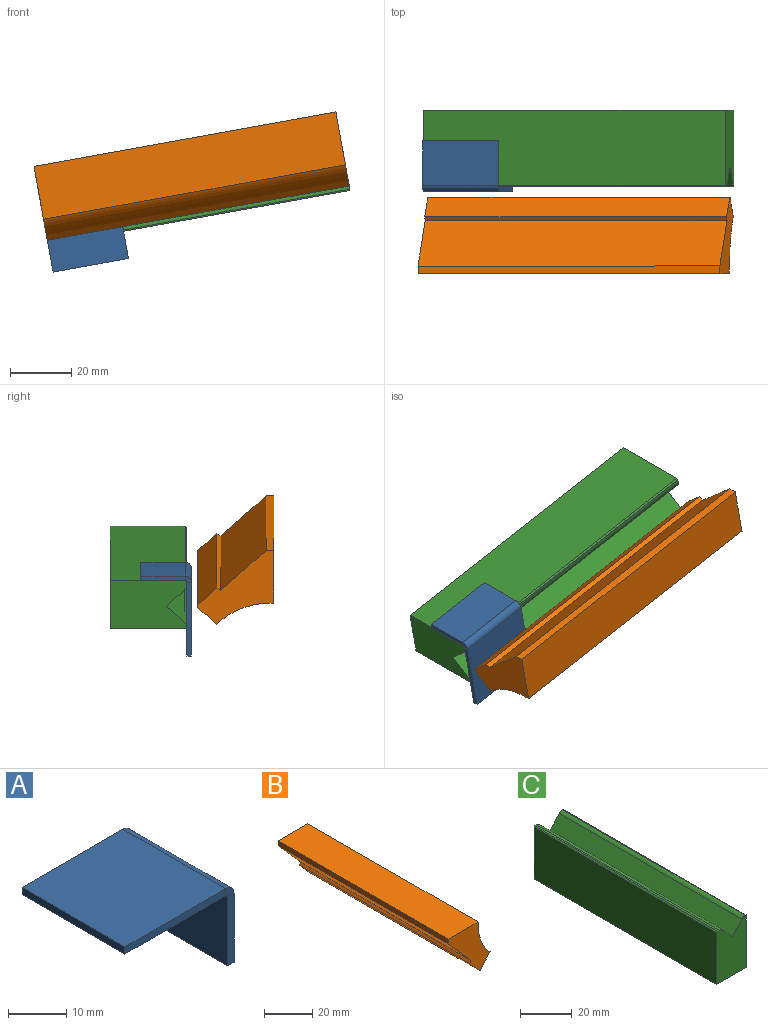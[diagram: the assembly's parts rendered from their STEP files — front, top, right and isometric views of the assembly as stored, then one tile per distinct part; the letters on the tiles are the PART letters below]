
ASSEMBLY  parts=3 mates=5
PART A: 14 faces, bbox 26.5x25x16.5 mm
  f0: plane 24.5x1.5mm, normal (0,1,0), area 36.8mm2, adj f2,f3,f4,f11
  f1: plane 24.5x1.5mm, normal (0,-1,0), area 36.8mm2, adj f2,f3,f4,f10
  f2: plane 25x1.5mm, normal (-1,0,0), area 37.5mm2, adj f0,f1,f3,f4
  f3: plane 25x24.5mm, normal (0,0,-1), area 612.5mm2, adj f0,f1,f2,f13
  f4: plane 25x24.5mm, normal (0,0,1), area 612.5mm2, adj f0,f1,f2,f12
  f5: plane 14.5x1.5mm, normal (0,1,0), area 21.7mm2, adj f6,f8,f9,f11
  f6: plane 25x1.5mm, normal (0,0,-1), area 37.5mm2, adj f5,f7,f8,f9
  f7: plane 14.5x1.5mm, normal (0,-1,0), area 21.7mm2, adj f6,f8,f9,f10
  f8: plane 25x14.5mm, normal (-1,0,0), area 362.5mm2, adj f5,f6,f7,f13
  f9: plane 25x14.5mm, normal (1,0,0), area 362.5mm2, adj f5,f6,f7,f12
  f10: plane 2x2mm, normal (0,-1,0), area 2.9mm2, adj f1,f7,f12,f13
  f11: plane 2x2mm, normal (0,1,0), area 2.9mm2, adj f0,f5,f12,f13
  f12: cylinder r=2mm len=25mm, axis (0,-1,0), area 78.5mm2, adj f4,f9,f10,f11
  f13: cylinder r=0.5mm len=25mm, axis (0,-1,0), area 19.6mm2, adj f3,f8,f10,f11
PART B: 11 faces, bbox 24.5x100x25 mm
  f0: cylinder r=0.6mm len=100mm, axis (0,1,0), area 100.5mm2, adj f1,f7,f8,f9
  f1: plane 100x6.16mm, normal (0.74,0,-0.67), area 829.1mm2, adj f0,f2,f8,f9
  f2: cylinder r=25mm len=100mm, axis (0,1,0), area 1916.6mm2, adj f1,f3,f8,f9
  f3: plane 100x1.3mm, normal (1,0,0), area 129.7mm2, adj f2,f8,f9,f10
  f4: plane 100x2.51mm, normal (-1,0,0), area 250.9mm2, adj f5,f8,f9,f10
  f5: plane 100x14.8mm, normal (-0.74,0,-0.67), area 1991.2mm2, adj f4,f6,f8,f9
  f6: plane 100x1.3mm, normal (-0.84,0,0.54), area 155.3mm2, adj f5,f7,f8,f9
  f7: plane 100x6.19mm, normal (-0.74,0,-0.67), area 833.4mm2, adj f0,f6,f8,f9
  f8: plane 25x24.49mm, normal (0,-1,0), area 288.1mm2, adj f0,f1,f2,f3,f4,f5,f6,f7
  f9: plane 25x24.49mm, normal (0,1,0), area 288.1mm2, adj f0,f1,f2,f3,f4,f5,f6,f7
  f10: plane 100x17.5mm, normal (0,0,1), area 1750mm2, adj f3,f4,f8,f9
PART C: 12 faces, bbox 16x100x25 mm
  f0: plane 100x25mm, normal (1,0,0), area 2500mm2, adj f2,f3,f4,f11
  f1: plane 100x24.5mm, normal (-1,0,0), area 2450mm2, adj f2,f3,f10,f11
  f2: plane 25x16mm, normal (0,-1,0), area 359.6mm2, adj f0,f1,f4,f5,f6,f7,f8,f9
  f3: plane 25x16mm, normal (0,1,0), area 359.6mm2, adj f0,f1,f4,f5,f6,f7,f8,f9
  f4: plane 100x0.39mm, normal (0,0,1), area 38.7mm2, adj f0,f2,f3,f5
  f5: cylinder r=2.5mm len=100mm, axis (0,1,0), area 209.4mm2, adj f2,f3,f4,f6
  f6: plane 100x5.84mm, normal (-0.74,0,0.67), area 785.4mm2, adj f2,f3,f5,f7
  f7: plane 100x5.84mm, normal (0.74,0,0.67), area 785.4mm2, adj f2,f3,f6,f8
  f8: cylinder r=2.5mm len=100mm, axis (0,1,0), area 209.4mm2, adj f2,f3,f7,f9
  f9: plane 100x0.89mm, normal (0,0,1), area 88.7mm2, adj f2,f3,f8,f10
  f10: plane 100x0.5mm, normal (-0.71,0,0.71), area 70.7mm2, adj f1,f2,f3,f9
  f11: plane 100x16mm, normal (0,0,-1), area 1600mm2, adj f0,f1,f2,f3
PLACE A rot(axis=(0.51,-0.61,0.61),126.1deg) t=(-113.23,73.45,-84.46)mm
PLACE B rot(axis=(0.65,0.54,-0.54),114.3deg) t=(-2.34,-64.04,-135.99)mm
PLACE C rot(axis=(0.65,0.54,-0.54),114.3deg) t=(-90.73,-152.91,354.81)mm
MATE planar A.f0 <-> C.f2  axis (-0.98,0,-0.18) through (-114.08,68.7,-79.73)mm
MATE planar C.f9 <-> A.f3  axis (0,-1,0) through (-67.04,69.45,-58.81)mm
MATE planar A.f8 <-> C.f1  axis (0.18,0,-0.98) through (-104.03,77.2,-64.97)mm
MATE planar C.f2 <-> B.f8  axis (-0.98,0,-0.18) through (-114.93,83.11,-75)mm
MATE fastened B.f8 <-> C.f2  axis (-0.98,0,-0.18) through (-114.83,66.11,-75.55)mm
